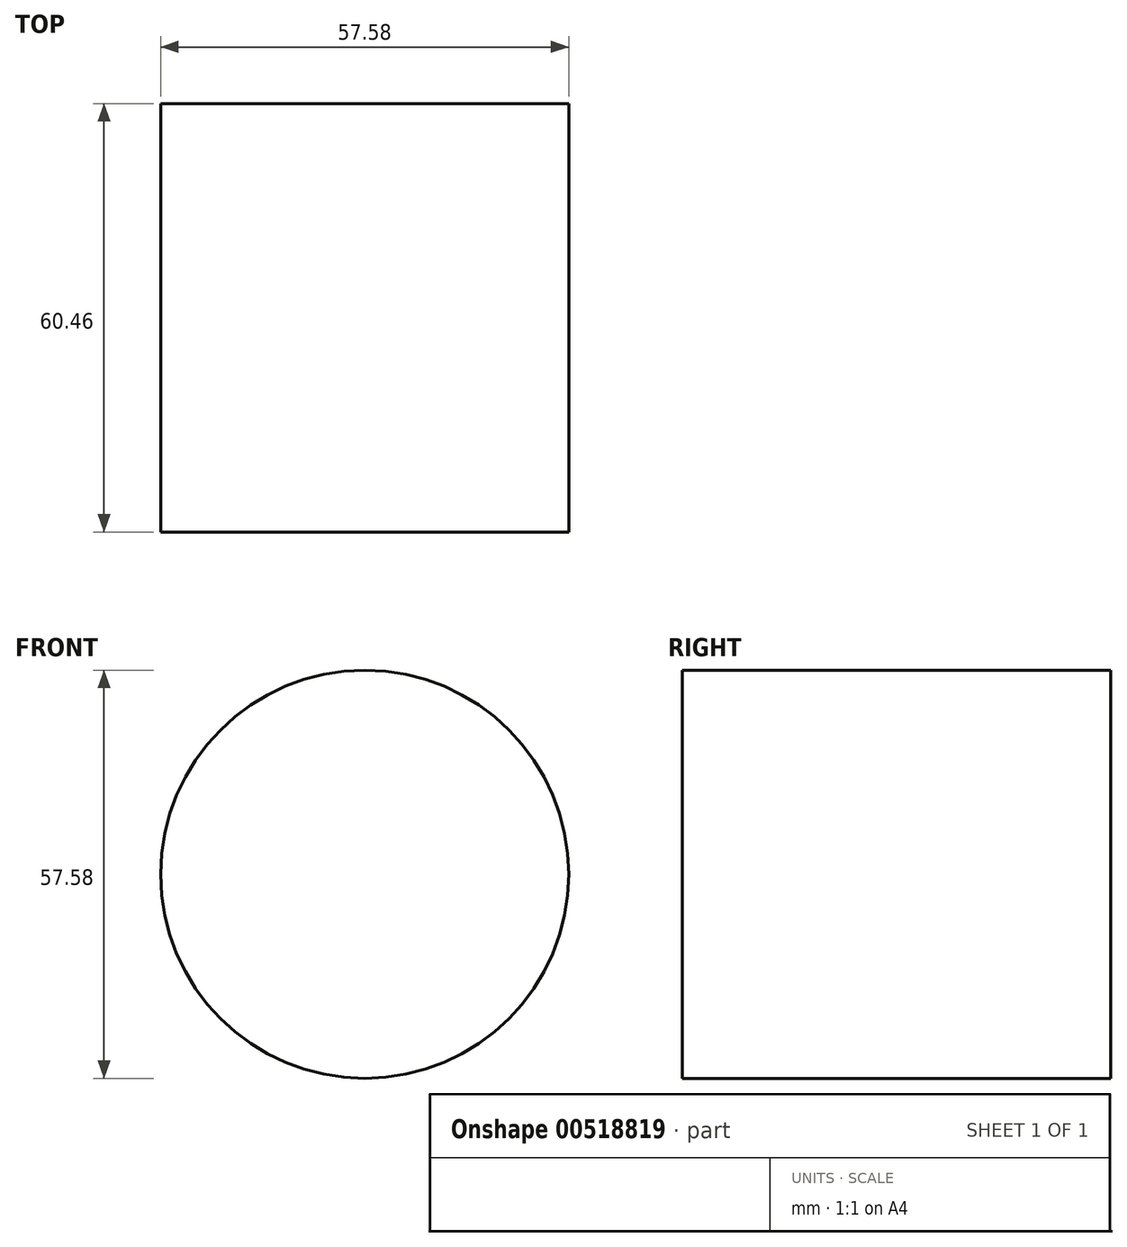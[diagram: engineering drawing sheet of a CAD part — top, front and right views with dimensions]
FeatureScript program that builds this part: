
annotation { "Feature Type Name" : "Feature", "Feature Type Description" : "" }
export const myFeature = defineFeature(function(context is Context, id is Id, definition is map)
    precondition{}
    {
        {
            var Q0;
            Q0=qCreatedBy(makeId("Front.planeOp"),FACE);
            var sketch = newSketch(context, id + "F0", { "sketchPlane" : qUnion([Q0])});
            skCircle(sketch, "E0", {"center": v(0, 0) * mm, "radius": 28.79 * mm});
            skSolve(sketch);
        }
        {
            var Q0;
            Q0 = qSketchRegion(id + "F0", true);
            extrude(context, id + "F1", {"entities" : qUnion([Q0]), "endBound" : BoundingType.SYMMETRIC, "depth" : 60.45 * mm, "offsetDistance" : 25.4 * mm});
        }
    });
